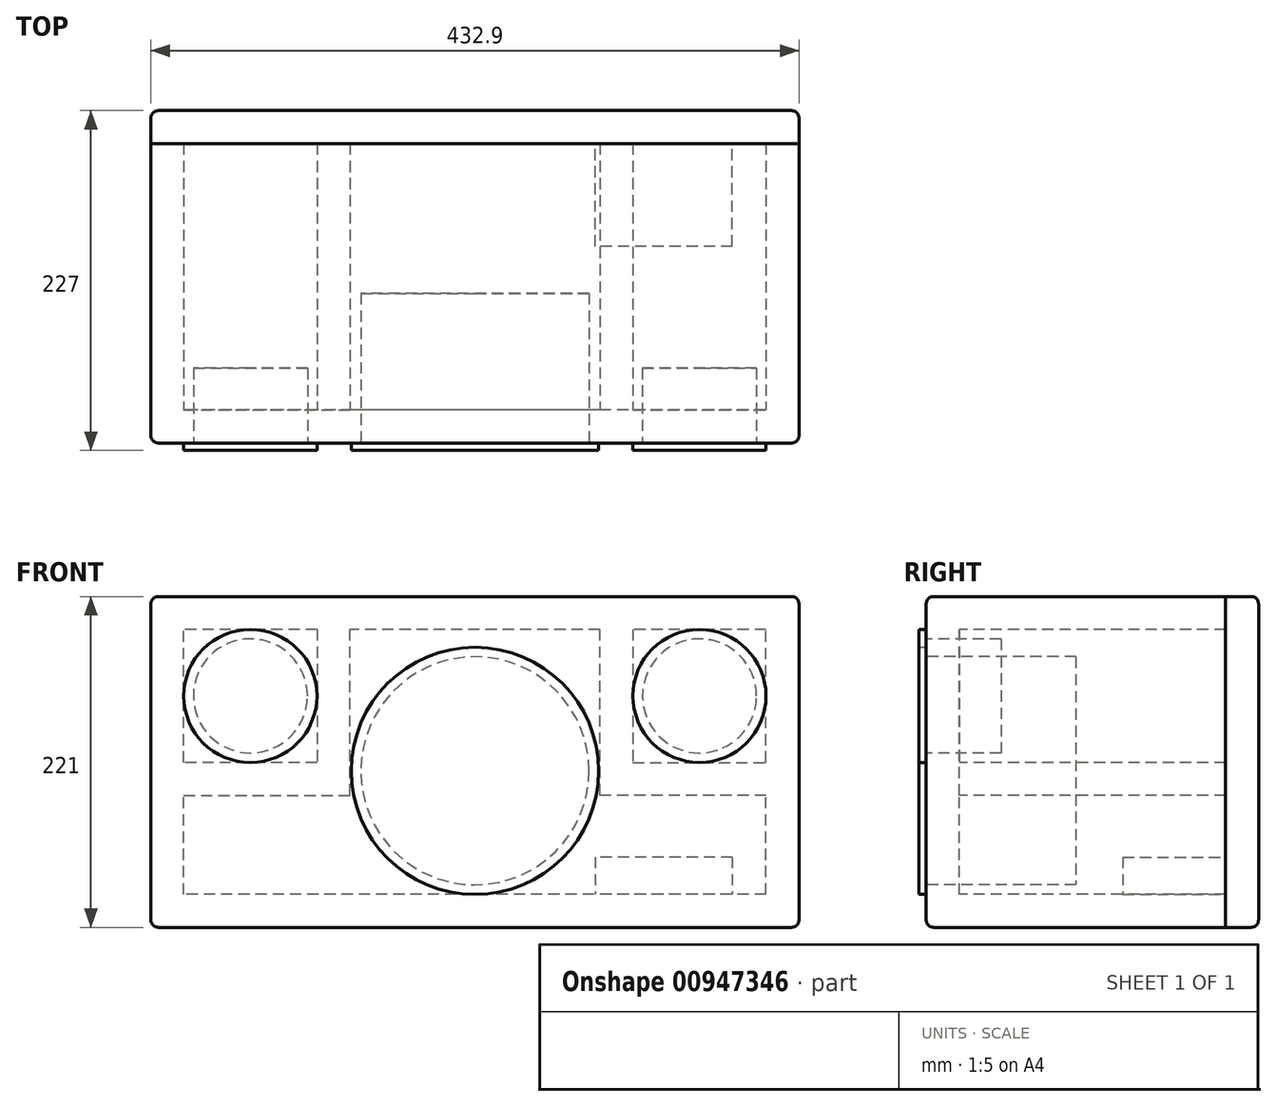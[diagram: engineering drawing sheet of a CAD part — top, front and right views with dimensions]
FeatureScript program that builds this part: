
annotation { "Feature Type Name" : "Feature", "Feature Type Description" : "" }
export const myFeature = defineFeature(function(context is Context, id is Id, definition is map)
    precondition{}
    {
        {
            assignVariable(context, id + "F0", {"name" : "WooferDepth", "anyValue" : 100});
        }
        {
            assignVariable(context, id + "F1", {"name" : "FRDepth", "anyValue" : 50});
        }
        {
            assignVariable(context, id + "F2", {"name" : "WoodThickness", "anyValue" : 22});
        }
        {
            var Q0;
            Q0=qCreatedBy(makeId("Front.planeOp"),FACE);
            var sketch = newSketch(context, id + "F3", { "sketchPlane" : qUnion([Q0])});
            skCircle(sketch, "E0", {"center": v(0, 0) * mm, "radius": 82.55 * mm});
            skSolve(sketch);
        }
        {
            var Q0;
            Q0 = qSketchRegion(id + "F3", true);
            extrude(context, id + "F4", {"entities" : qUnion([Q0]), "depth" : 5 * mm, "offsetDistance" : 25 * mm});
        }
        {
            var Q0;
            Q0=makeQuery(id+"F4.opExtrude","CAP_FACE",FACE,{"disambiguationData":[OSD([sQuery(id+"F3.wireOp",EDGE,"E0")])],"isStart":true});
            var sketch = newSketch(context, id + "F5", { "sketchPlane" : qUnion([Q0])});
            skCircle(sketch, "E1", {"center": v(0, 0) * mm, "radius": 76.2 * mm});
            skSolve(sketch);
        }
        {
            var Q0;
            Q0 = qSketchRegion(id + "F5", true);
            extrude(context, id + "F6", {"entities" : qUnion([Q0]), "operationType" : NewBodyOperationType.ADD, "depth" : (getVariable(context, 'WooferDepth')) * mm, "offsetDistance" : 25 * mm});
        }
        {
            var Q0;
            Q0=qCreatedBy(makeId("Front.planeOp"),FACE);
            var sketch = newSketch(context, id + "F7", { "sketchPlane" : qUnion([Q0])});
            skCircle(sketch, "E2", {"center": v(150, 50) * mm, "radius": 44.45 * mm});
            skSolve(sketch);
        }
        {
            var Q0;
            Q0 = qSketchRegion(id + "F7", true);
            extrude(context, id + "F8", {"entities" : qUnion([Q0]), "depth" : 5 * mm, "offsetDistance" : 25 * mm});
        }
        {
            var Q0;
            Q0=makeQuery(id+"F8.opExtrude","CAP_FACE",FACE,{"disambiguationData":[OSD([sQuery(id+"F7.wireOp",EDGE,"E2")])],"isStart":true});
            var sketch = newSketch(context, id + "F9", { "sketchPlane" : qUnion([Q0])});
            skCircle(sketch, "E3.0.0", {"center": v(-150, 50) * mm, "radius": 44.45 * mm, "construction": true});
            skCircle(sketch, "E4", {"center": v(-150, 50) * mm, "radius": 38.1 * mm});
            skSolve(sketch);
        }
        {
            var Q0;
            Q0 = qSketchRegion(id + "F9", true);
            extrude(context, id + "F10", {"entities" : qUnion([Q0]), "operationType" : NewBodyOperationType.ADD, "depth" : (getVariable(context, 'FRDepth')) * mm, "offsetDistance" : 25 * mm});
        }
        {
            var Q0;
            Q0=makeQuery(id+"F8.opExtrude","SWEPT_BODY",BODY,{"disambiguationData":[OSD([sQuery(id+"F7.wireOp",EDGE,"E2")])]});
            var Q1;
            Q1=qCreatedBy(makeId("Right.planeOp"),FACE);
            mirror(context, id + "F11", {"entities" : qUnion([Q0]), "mirrorPlane" : qUnion([Q1])});
        }
        {
            var Q0;
            Q0=qCreatedBy(makeId("Front.planeOp"),FACE);
            var sketch = newSketch(context, id + "F12", { "sketchPlane" : qUnion([Q0])});
            skLineSegment(sketch, "E5.bottom", {"start": v(216.45, -104.55) * mm, "end": v(-216.45, -104.55) * mm});
            skLineSegment(sketch, "E5.top", {"start": v(216.45, 116.45) * mm, "end": v(-216.45, 116.45) * mm});
            skLineSegment(sketch, "E5.left", {"start": v(216.45, -104.55) * mm, "end": v(216.45, 116.45) * mm});
            skLineSegment(sketch, "E5.right", {"start": v(-216.45, -104.55) * mm, "end": v(-216.45, 116.45) * mm});
            skPoint(sketch, "E5.middle", {"position": v(0, 5.95) * mm});
            skLineSegment(sketch, "E6", {"start": v(-85.23, -82.55) * mm, "end": v(135.12, -82.55) * mm, "construction": true});
            skLineSegment(sketch, "E7", {"start": v(194.45, 115.37) * mm, "end": v(194.45, -23.9) * mm, "construction": true});
            skLineSegment(sketch, "E8", {"start": v(40.19, 94.45) * mm, "end": v(177.38, 94.45) * mm, "construction": true});
            skSolve(sketch);
        }
        {
            var Q0;
            Q0 = qSketchRegion(id + "F12", true);
            extrude(context, id + "F13", {"entities" : qUnion([Q0]), "oppositeDirection" : true, "depth" : 200 * mm, "offsetDistance" : 25 * mm});
        }
        {
            var Q0;
            Q0=makeQuery(id+"F13.opExtrude","CAP_FACE",FACE,{"disambiguationData":[OSD([sQuery(id+"F12.wireOp",EDGE,"E5.bottom"),sQuery(id+"F12.wireOp",EDGE,"E5.top"),sQuery(id+"F12.wireOp",EDGE,"E5.left"),sQuery(id+"F12.wireOp",EDGE,"E5.right")])],"isStart":false});
            shell(context, id + "F14", {"entities" : qUnion([Q0]), "thickness" : (getVariable(context, 'WoodThickness')) * mm});
        }
        {
            var Q0;
            Q0=makeQuery(id+"F14.opShell","OFFSET_FACE",FACE,{"disambiguationData":[OSD([sQuery(id+"F12.wireOp",EDGE,"E5.bottom"),sQuery(id+"F12.wireOp",EDGE,"E5.top"),sQuery(id+"F12.wireOp",EDGE,"E5.left"),sQuery(id+"F12.wireOp",EDGE,"E5.right")])]});
            var sketch = newSketch(context, id + "F15", { "sketchPlane" : qUnion([Q0])});
            skLineSegment(sketch, "E9", {"start": v(-105.55, 94.45) * mm, "end": v(-105.55, 5.55) * mm});
            skLineSegment(sketch, "E10", {"start": v(-105.55, 5.55) * mm, "end": v(-194.45, 5.55) * mm});
            skLineSegment(sketch, "E11", {"start": v(-194.45, 5.55) * mm, "end": v(-194.45, -16.45) * mm});
            skLineSegment(sketch, "E12", {"start": v(-194.45, -16.45) * mm, "end": v(-83.55, -16.45) * mm});
            skLineSegment(sketch, "E13", {"start": v(-83.55, -16.45) * mm, "end": v(-83.55, 94.45) * mm});
            skLineSegment(sketch, "E14", {"start": v(-83.55, 94.45) * mm, "end": v(-105.55, 94.45) * mm});
            skCircle(sketch, "E15.0.0", {"center": v(-150, 50) * mm, "radius": 38.1 * mm, "construction": true});
            skLineSegment(sketch, "E16", {"start": v(-150, 50) * mm, "end": v(-150, 94.45) * mm, "construction": true});
            skLineSegment(sketch, "E17", {"start": v(-150, 50) * mm, "end": v(-105.55, 50) * mm, "construction": true});
            skSolve(sketch);
        }
        {
            var Q0;
            Q0 = qSketchRegion(id + "F15", true);
            var Q1;
            Q1=makeQuery(id+"F13.opExtrude","CAP_FACE",FACE,{"disambiguationData":[OSD([sQuery(id+"F12.wireOp",EDGE,"E5.bottom"),sQuery(id+"F12.wireOp",EDGE,"E5.top"),sQuery(id+"F12.wireOp",EDGE,"E5.left"),sQuery(id+"F12.wireOp",EDGE,"E5.right")])],"isStart":false});
            extrude(context, id + "F16", {"entities" : qUnion([Q0]), "endBound" : BoundingType.UP_TO_SURFACE, "depth" : 25 * mm, "endBoundEntityFace" : qUnion([Q1]), "offsetDistance" : 25 * mm});
        }
        {
            var Q0;
            Q0=makeQuery(id+"F16.opExtrude","SWEPT_BODY",BODY,{"disambiguationData":[OSD([sQuery(id+"F15.wireOp",EDGE,"E9"),sQuery(id+"F15.wireOp",EDGE,"E10"),sQuery(id+"F15.wireOp",EDGE,"E11"),sQuery(id+"F15.wireOp",EDGE,"E12"),sQuery(id+"F15.wireOp",EDGE,"E13"),sQuery(id+"F15.wireOp",EDGE,"E14")])]});
            var Q1;
            Q1=qCreatedBy(makeId("Right.planeOp"),FACE);
            mirror(context, id + "F17", {"operationType" : NewBodyOperationType.ADD, "entities" : qUnion([Q0]), "mirrorPlane" : qUnion([Q1])});
        }
        {
            var Q0;
            Q0=makeQuery(id+"F14.opShell","OFFSET_FACE",FACE,{"disambiguationData":[OSD([sQuery(id+"F12.wireOp",EDGE,"E5.bottom")])]});
            var sketch = newSketch(context, id + "F18", { "sketchPlane" : qUnion([Q0])});
            skLineSegment(sketch, "E18.bottom", {"start": v(171.93, 131.42) * mm, "end": v(80.5, 131.42) * mm});
            skLineSegment(sketch, "E18.top", {"start": v(171.93, 200) * mm, "end": v(80.5, 200) * mm});
            skLineSegment(sketch, "E18.left", {"start": v(171.93, 131.42) * mm, "end": v(171.93, 200) * mm});
            skLineSegment(sketch, "E18.right", {"start": v(80.5, 131.42) * mm, "end": v(80.5, 200) * mm});
            skSolve(sketch);
        }
        {
            var Q0;
            Q0 = qSketchRegion(id + "F18", true);
            extrude(context, id + "F19", {"entities" : qUnion([Q0]), "depth" : 25 * mm, "offsetDistance" : 25 * mm});
        }
        {
            var Q0;
            {var subQ0=makeQuery(id+"F16.opExtrude","CAP_FACE",FACE,{"disambiguationData":[OSD([sQuery(id+"F15.wireOp",EDGE,"E9"),sQuery(id+"F15.wireOp",EDGE,"E10"),sQuery(id+"F15.wireOp",EDGE,"E11"),sQuery(id+"F15.wireOp",EDGE,"E12"),sQuery(id+"F15.wireOp",EDGE,"E13"),sQuery(id+"F15.wireOp",EDGE,"E14")])],"isStart":false});Q0=makeQuery(id+"F17.boolean.opBoolean","MERGE",FACE,{"derivedFrom":[makeQuery(id+"F13.opExtrude","CAP_FACE",FACE,{"disambiguationData":[OSD([sQuery(id+"F12.wireOp",EDGE,"E5.bottom"),sQuery(id+"F12.wireOp",EDGE,"E5.top"),sQuery(id+"F12.wireOp",EDGE,"E5.left"),sQuery(id+"F12.wireOp",EDGE,"E5.right")])],"isStart":false}),subQ0,makeQuery(id+"F17.opPattern","COPY",FACE,{"derivedFrom":subQ0,"instanceName":"1"})]});}
            var sketch = newSketch(context, id + "F20", { "sketchPlane" : qUnion([Q0])});
            skLineSegment(sketch, "E19.bottom", {"start": v(-216.45, 116.45) * mm, "end": v(216.45, 116.45) * mm});
            skLineSegment(sketch, "E19.top", {"start": v(-216.45, -104.55) * mm, "end": v(216.45, -104.55) * mm});
            skLineSegment(sketch, "E19.left", {"start": v(-216.45, 116.45) * mm, "end": v(-216.45, -104.55) * mm});
            skLineSegment(sketch, "E19.right", {"start": v(216.45, 116.45) * mm, "end": v(216.45, -104.55) * mm});
            skSolve(sketch);
        }
        {
            var Q0;
            Q0 = qSketchRegion(id + "F20", true);
            extrude(context, id + "F21", {"entities" : qUnion([Q0]), "depth" : 22 * mm, "offsetDistance" : 25 * mm});
        }
        {
            var Q0;
            Q0=makeQuery(id+"F21.opExtrude","CAP_FACE",FACE,{"disambiguationData":[OSD([sQuery(id+"F20.wireOp",EDGE,"E19.bottom"),sQuery(id+"F20.wireOp",EDGE,"E19.top"),sQuery(id+"F20.wireOp",EDGE,"E19.left"),sQuery(id+"F20.wireOp",EDGE,"E19.right")])],"isStart":false});
            var Q1;
            Q1=makeQuery(id+"F13.opExtrude","SWEPT_EDGE",EDGE,{"disambiguationData":[OSD([sQuery(id+"F12.wireOp",EDGE,"E5.top"),sQuery(id+"F12.wireOp",EDGE,"E5.left")])]});
            var Q2;
            Q2=makeQuery(id+"F21.opExtrude","SWEPT_EDGE",EDGE,{"disambiguationData":[OSD([sQuery(id+"F20.wireOp",EDGE,"E19.bottom"),sQuery(id+"F20.wireOp",EDGE,"E19.left")])]});
            var Q3;
            Q3=makeQuery(id+"F21.opExtrude","SWEPT_EDGE",EDGE,{"disambiguationData":[OSD([sQuery(id+"F20.wireOp",EDGE,"E19.top"),sQuery(id+"F20.wireOp",EDGE,"E19.left")])]});
            var Q4;
            Q4=makeQuery(id+"F13.opExtrude","SWEPT_EDGE",EDGE,{"disambiguationData":[OSD([sQuery(id+"F12.wireOp",EDGE,"E5.bottom"),sQuery(id+"F12.wireOp",EDGE,"E5.left")])]});
            var Q5;
            Q5=makeQuery(id+"F13.opExtrude","CAP_EDGE",EDGE,{"disambiguationData":[OSD([sQuery(id+"F12.wireOp",EDGE,"E5.left")])],"isStart":true});
            var Q6;
            Q6=makeQuery(id+"F21.opExtrude","SWEPT_EDGE",EDGE,{"disambiguationData":[OSD([sQuery(id+"F20.wireOp",EDGE,"E19.bottom"),sQuery(id+"F20.wireOp",EDGE,"E19.right")])]});
            var Q7;
            Q7=makeQuery(id+"F13.opExtrude","SWEPT_EDGE",EDGE,{"disambiguationData":[OSD([sQuery(id+"F12.wireOp",EDGE,"E5.top"),sQuery(id+"F12.wireOp",EDGE,"E5.right")])]});
            var Q8;
            Q8=makeQuery(id+"F21.opExtrude","SWEPT_EDGE",EDGE,{"disambiguationData":[OSD([sQuery(id+"F20.wireOp",EDGE,"E19.top"),sQuery(id+"F20.wireOp",EDGE,"E19.right")])]});
            var Q9;
            Q9=makeQuery(id+"F13.opExtrude","SWEPT_EDGE",EDGE,{"disambiguationData":[OSD([sQuery(id+"F12.wireOp",EDGE,"E5.bottom"),sQuery(id+"F12.wireOp",EDGE,"E5.right")])]});
            var Q10;
            Q10=makeQuery(id+"F13.opExtrude","CAP_EDGE",EDGE,{"disambiguationData":[OSD([sQuery(id+"F12.wireOp",EDGE,"E5.right")])],"isStart":true});
            var Q11;
            Q11=makeQuery(id+"F13.opExtrude","CAP_EDGE",EDGE,{"disambiguationData":[OSD([sQuery(id+"F12.wireOp",EDGE,"E5.top")])],"isStart":true});
            var Q12;
            Q12=makeQuery(id+"F13.opExtrude","CAP_EDGE",EDGE,{"disambiguationData":[OSD([sQuery(id+"F12.wireOp",EDGE,"E5.bottom")])],"isStart":true});
            fillet(context, id + "F22", {"entities" : qUnion([Q0, Q1, Q2, Q3, Q4, Q5, Q6, Q7, Q8, Q9, Q10, Q11, Q12]), "radius" : 5 * mm, "tangentPropagation" : true, "allowEdgeOverflow" : false});
        }
    });
